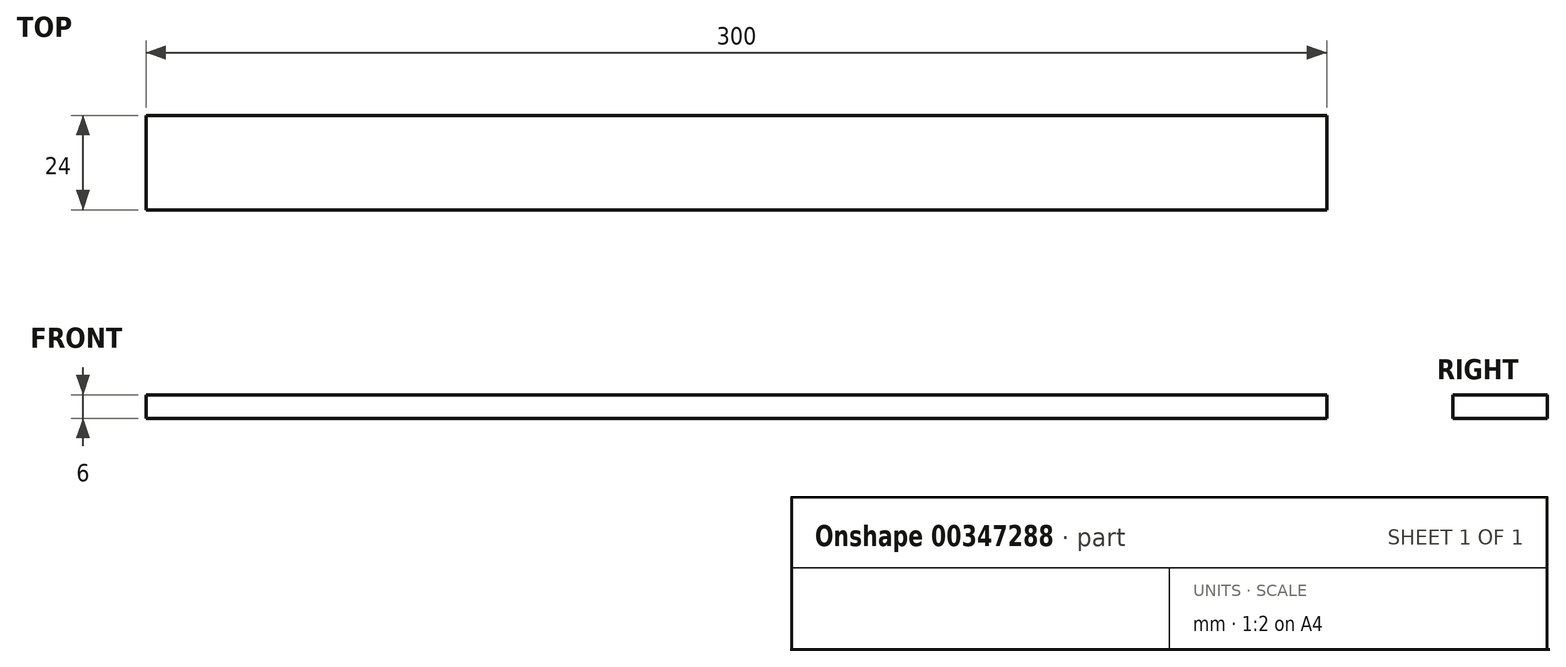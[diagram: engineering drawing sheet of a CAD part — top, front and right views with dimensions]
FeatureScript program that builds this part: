
annotation { "Feature Type Name" : "Feature", "Feature Type Description" : "" }
export const myFeature = defineFeature(function(context is Context, id is Id, definition is map)
    precondition{}
    {
        {
            var Q0;
            Q0=qCreatedBy(makeId("Right.planeOp"),FACE);
            var sketch = newSketch(context, id + "F0", { "sketchPlane" : qUnion([Q0])});
            skLineSegment(sketch, "E0.bottom", {"start": v(0, 0) * mm, "end": v(24, 0) * mm});
            skLineSegment(sketch, "E0.top", {"start": v(0, 6) * mm, "end": v(24, 6) * mm});
            skLineSegment(sketch, "E0.left", {"start": v(0, 0) * mm, "end": v(0, 6) * mm});
            skLineSegment(sketch, "E0.right", {"start": v(24, 0) * mm, "end": v(24, 6) * mm});
            skSolve(sketch);
        }
        {
            var Q0;
            Q0 = qSketchRegion(id + "F0", true);
            extrude(context, id + "F1", {"entities" : qUnion([Q0]), "depth" : 300 * mm});
        }
    });
